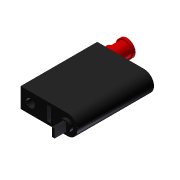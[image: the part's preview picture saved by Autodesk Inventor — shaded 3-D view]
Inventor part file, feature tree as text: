
AUTODESK INVENTOR PART (.ipt)
format: ipt  version: 2011 (Build 150239000, 239)  size: 140,800 bytes
history: native  units: in
note: dims shown in document units (in); Inventor stores cm internally (conversion verified against a paired STEP export)
features: extrude x6, sketch x6
ambient origin geometry x8: Origin, YZ Plane, XZ Plane, XY Plane, X Axis, Y Axis, Z Axis, Center Point
bodies: Solid1 (feature_tree)
feature tree (12):
  extrude  "Extrusion1"  Depth=0.35in
  extrude  "Extrusion2"  TaperAngle=0.0deg  [1 undecoded]
  extrude  "Extrusion3"  Depth=0.15in
  extrude  "Extrusion4"  Depth=0.175in
  extrude  "Extrusion5"  Depth=0.2875in
  extrude  "Extrusion6"  Depth=0.25in
  sketch  "Sketch1"  dims[d0=1.0in d1=0.35in]
  sketch  "Sketch2"  dims[d2=0.0in d3=0.0in]
  sketch  "Sketch3"  dims[d4=0.15in d5=0.15in]
  sketch  "Sketch4"  dims[d6=0.0in d7=0.175in]
  sketch  "Sketch5"  dims[d8=0.175in d9=0.2875in]
  sketch  "Sketch6"  dims[d12=0.075in d13=0.25in d17=1.35in d18=0.0in d19=0.3in d20=0.1in d21=0.0in d22=0.25in d23=0.2in d24=0.0in d25=0.05in d26=0.0in d27=0.2in d28=0.05in d29=0.0in d30=0.15in d31=0.05in d32=0.025in d33=0.075in d34=0.2in d35=0.0in]
note: 1 required parameter value undecoded (feature->parameter linkage not recoverable at this tier; creation-order binding heuristic only, values carry confidence <= 0.55)
